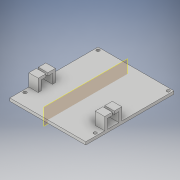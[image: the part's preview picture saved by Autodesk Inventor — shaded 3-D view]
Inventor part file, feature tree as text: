
AUTODESK INVENTOR PART (.ipt)
format: ipt  version: 2018 (Build 220112000, 112)  size: 161,280 bytes
history: native  units: mm
features: extrude x3, sketch x3, mirror x2, plane x1
ambient origin geometry x8: Origin, YZ Plane, XZ Plane, XY Plane, X Axis, Y Axis, Z Axis, Center Point
bodies: Solid1 (feature_tree)
feature tree (9):
  extrude  "Extrusion1"  Depth=93.0mm
  sketch  "Sketch3"  dims[d2=3.0mm d3=0.0mm d4=3.0mm]
  plane  "Work Plane1"
  extrude  "Extrusion2"  Depth=3.0mm
  mirror  "Mirror1"
  extrude  "Extrusion3"  Depth=20.0mm
  mirror  "Mirror2"
  sketch  "Sketch1"  dims[d0=80.0mm d1=93.0mm]
  sketch  "Sketch4"  dims[d5=3.0mm d6=20.0mm d7=12.0mm d8=10.0mm d9=3.0mm d10=5.0mm d11=5.0mm d12=3.0mm d13=10.0mm d14=0.0mm d15=3.2mm d16=3.0mm d17=13.0mm d18=3.0mm d19=10.0mm d20=0.0mm]
